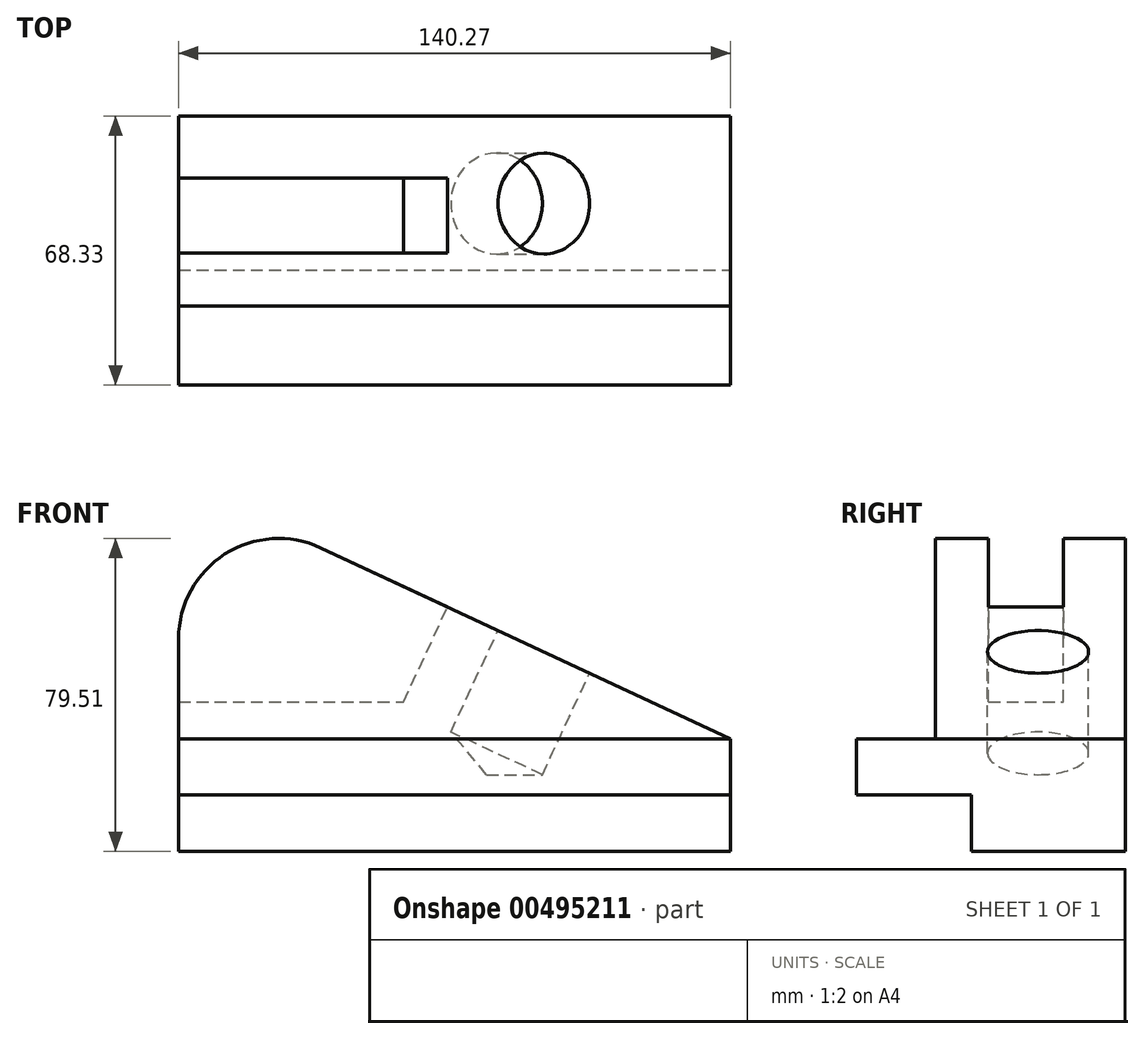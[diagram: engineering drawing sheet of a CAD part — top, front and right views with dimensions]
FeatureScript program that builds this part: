
annotation { "Feature Type Name" : "Feature", "Feature Type Description" : "" }
export const myFeature = defineFeature(function(context is Context, id is Id, definition is map)
    precondition{}
    {
        {
            var Q0;
            Q0=qCreatedBy(makeId("Front.planeOp"),FACE);
            var sketch = newSketch(context, id + "F0", { "sketchPlane" : qUnion([Q0])});
            skLineSegment(sketch, "E0", {"start": v(0, 0) * mm, "end": v(0, 28.58) * mm});
            skLineSegment(sketch, "E1", {"start": v(-140.27, 54.11) * mm, "end": v(-140.27, 0) * mm});
            skLineSegment(sketch, "E2", {"start": v(-140.27, 0) * mm, "end": v(0, 0) * mm});
            skLineSegment(sketch, "E3", {"start": v(0, 28.58) * mm, "end": v(-104.14, 77.13) * mm});
            skArc(sketch, "E4.filletArc", {"start": v(-104.14, 77.13) * mm, "mid": v(-128.52, 75.54) * mm, "end": v(-140.27, 54.11) * mm});
            skSolve(sketch);
        }
        {
            var Q0;
            Q0 = qSketchRegion(id + "F0", true);
            extrude(context, id + "F1", {"entities" : qUnion([Q0]), "depth" : 68.33 * mm});
        }
        {
            var Q0;
            Q0=makeQuery(id+"F1.opExtrude","SWEPT_FACE",FACE,{"disambiguationData":[OSD([sQuery(id+"F0.wireOp",EDGE,"E0")])]});
            var sketch = newSketch(context, id + "F2", { "sketchPlane" : qUnion([Q0])});
            skLineSegment(sketch, "E5", {"start": v(-39.12, 0) * mm, "end": v(-39.12, 14.35) * mm});
            skLineSegment(sketch, "E6", {"start": v(-39.12, 14.35) * mm, "end": v(-68.33, 14.35) * mm});
            skLineSegment(sketch, "E7", {"start": v(-68.33, 14.35) * mm, "end": v(-68.33, 28.58) * mm});
            skLineSegment(sketch, "E8", {"start": v(-68.33, 28.58) * mm, "end": v(-48.26, 28.58) * mm});
            skLineSegment(sketch, "E9", {"start": v(-48.26, 28.58) * mm, "end": v(-48.26, 79.63) * mm});
            skLineSegment(sketch, "E10", {"start": v(-68.33, 0) * mm, "end": v(-39.12, 0) * mm});
            skLineSegment(sketch, "E11", {"start": v(-68.33, 0) * mm, "end": v(-68.33, 79.63) * mm});
            skLineSegment(sketch, "E12", {"start": v(-68.33, 79.63) * mm, "end": v(-48.26, 79.63) * mm});
            skSolve(sketch);
        }
        {
            var Q0;
            Q0 = qSketchRegion(id + "F2", true);
            extrude(context, id + "F3", {"entities" : qUnion([Q0]), "operationType" : NewBodyOperationType.REMOVE, "endBound" : BoundingType.THROUGH_ALL, "oppositeDirection" : true, "depth" : 25.4 * mm});
        }
        {
            var Q0;
            Q0=qCreatedBy(makeId("Front.planeOp"),FACE);
            cPlane(context, id + "F4", {"entities" : qUnion([Q0]), "cplaneType" : CPlaneType.OFFSET, "offset" : 22.22 * mm, "width" : 152.4 * mm, "height" : 152.4 * mm});
        }
        {
            var Q0;
            Q0=qCreatedBy(id+"F4.planeOp",FACE);
            var sketch = newSketch(context, id + "F5", { "sketchPlane" : qUnion([Q0])});
            skLineSegment(sketch, "E13", {"start": v(-62.02, 19.5) * mm, "end": v(-47.47, 50.7) * mm});
            skLineSegment(sketch, "E14", {"start": v(-59.1, 56.13) * mm, "end": v(-71.12, 30.35) * mm});
            skLineSegment(sketch, "E15", {"start": v(-71.12, 30.35) * mm, "end": v(-62.02, 19.5) * mm});
            skLineSegment(sketch, "E16", {"start": v(-59.1, 56.13) * mm, "end": v(-47.47, 50.7) * mm});
            skSolve(sketch);
        }
        {
            var Q0;
            Q0 = qSketchRegion(id + "F5", true);
            var Q1;
            Q1=sQuery(id+"F5.wireOp",EDGE,"E13");
            revolve(context, id + "F6", {"operationType" : NewBodyOperationType.REMOVE, "entities" : qUnion([Q0]), "axis" : qUnion([Q1]), "revolveType" : RevolveType.FULL, "oppositeDirection" : true});
        }
        {
            var Q0;
            Q0=qCreatedBy(makeId("Front.planeOp"),FACE);
            cPlane(context, id + "F7", {"entities" : qUnion([Q0]), "cplaneType" : CPlaneType.OFFSET, "offset" : 15.75 * mm, "width" : 152.4 * mm, "height" : 152.4 * mm});
        }
        {
            var Q0;
            Q0=qCreatedBy(id+"F7.planeOp",FACE);
            var sketch = newSketch(context, id + "F8", { "sketchPlane" : qUnion([Q0])});
            skLineSegment(sketch, "E17", {"start": v(-140.27, 38.05) * mm, "end": v(-83.12, 38.05) * mm});
            skLineSegment(sketch, "E18", {"start": v(-83.12, 38.05) * mm, "end": v(-71.9, 62.1) * mm});
            skLineSegment(sketch, "E19", {"start": v(-140.27, 38.05) * mm, "end": v(-140.27, 82.04) * mm});
            skLineSegment(sketch, "E20", {"start": v(-140.27, 82.04) * mm, "end": v(-71.9, 82.04) * mm});
            skLineSegment(sketch, "E21", {"start": v(-71.9, 82.04) * mm, "end": v(-71.9, 62.1) * mm});
            skSolve(sketch);
        }
        {
            var Q0;
            Q0 = qSketchRegion(id + "F8", true);
            extrude(context, id + "F9", {"entities" : qUnion([Q0]), "operationType" : NewBodyOperationType.REMOVE, "depth" : 19.05 * mm});
        }
    });
